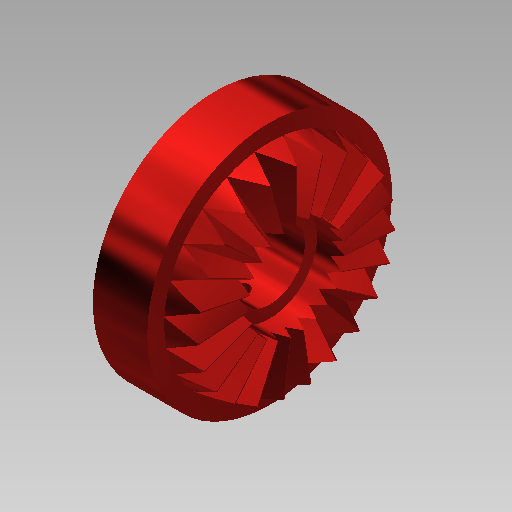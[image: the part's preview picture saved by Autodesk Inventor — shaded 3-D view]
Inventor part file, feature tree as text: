
AUTODESK INVENTOR PART (.ipt)
format: ipt  version: 2018.1 (Build 221171000, 171)  size: 322,560 bytes
history: native  units: in
note: dims shown in document units (in); Inventor stores cm internally (conversion verified against a paired STEP export)
features: sketch x5, extrude x4, revolve x1, pattern_circular x1, plane x1
ambient origin geometry x8: Origin, YZ Plane, XZ Plane, XY Plane, X Axis, Y Axis, Z Axis, Center Point
bodies: Solid1 (feature_tree)
feature tree (12):
  revolve  "Revolution1"  [1 undecoded]
  extrude  "Extrusion2"  Depth=0.2047in
  pattern_circular  "Circular Pattern1"  [2 undecoded]
  extrude  "Extrusion3"  Depth=0.1575in TaperAngle=0.0deg
  plane  "Work Plane2"
  extrude  "Extrusion4"  [1 undecoded]
  extrude  "Extrusion5"  [1 undecoded]
  sketch  "Sketch1"  dims[d5=90.0deg d12=0.0787in d13=-0.1787in]
  sketch  "Sketch3"  dims[d14=9.0551in d15=360.0deg d17=0.2047in]
  sketch  "Sketch4"  dims[d18=0.3937in d19=0.0in]
  sketch  "Sketch5"  dims[d20=0.2362in]
  sketch  "Sketch6"  dims[d21=0.2756in d22=0.0787in d23=0.0in d26=0.1575in d27=0.0in]
note: 5 required parameter values undecoded (feature->parameter linkage not recoverable at this tier; creation-order binding heuristic only, values carry confidence <= 0.55)